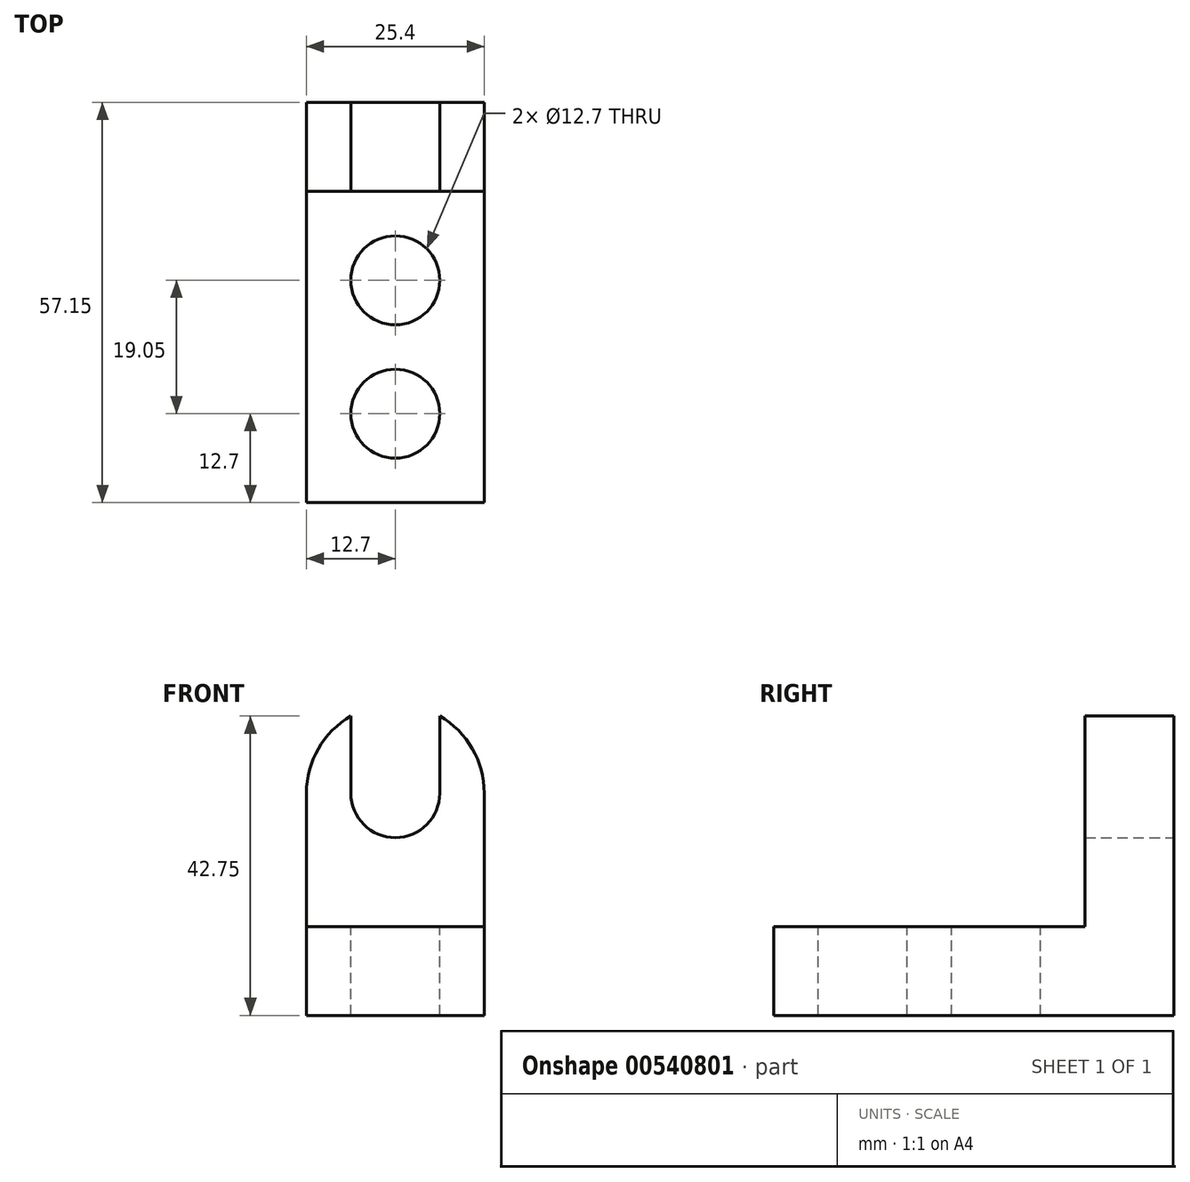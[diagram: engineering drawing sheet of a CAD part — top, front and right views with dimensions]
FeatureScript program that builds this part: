
annotation { "Feature Type Name" : "Feature", "Feature Type Description" : "" }
export const myFeature = defineFeature(function(context is Context, id is Id, definition is map)
    precondition{}
    {
        {
            var Q0;
            Q0=qCreatedBy(makeId("Top.planeOp"),FACE);
            var sketch = newSketch(context, id + "F0", { "sketchPlane" : qUnion([Q0])});
            skLineSegment(sketch, "E0", {"start": v(0, 0) * mm, "end": v(0, 57.15) * mm});
            skLineSegment(sketch, "E1", {"start": v(0, 57.15) * mm, "end": v(25.4, 57.15) * mm});
            skLineSegment(sketch, "E2", {"start": v(25.4, 57.15) * mm, "end": v(25.4, 0) * mm});
            skLineSegment(sketch, "E3", {"start": v(25.4, 0) * mm, "end": v(0, 0) * mm});
            skSolve(sketch);
        }
        {
            var Q0;
            Q0=makeQuery(id+"F0.imprint","IMPRINT",FACE,{"disambiguationData":[TD([[makeQuery(id+"F0.imprint","IMPRINT",EDGE,{"derivedFrom":sQuery(id+"F0.wireOp",EDGE,"E0")}),-1.0]])]});
            extrude(context, id + "F1", {"entities" : qUnion([Q0]), "depth" : 44.45 * mm, "offsetDistance" : 25.4 * mm});
        }
        {
            var Q0;
            Q0=makeQuery(id+"F1.opExtrude","SWEPT_FACE",FACE,{"disambiguationData":[OSD([sQuery(id+"F0.wireOp",EDGE,"E0")])]});
            var sketch = newSketch(context, id + "F2", { "sketchPlane" : qUnion([Q0])});
            skLineSegment(sketch, "E4", {"start": v(-44.45, 44.45) * mm, "end": v(-44.45, 12.7) * mm});
            skLineSegment(sketch, "E5", {"start": v(-44.45, 12.7) * mm, "end": v(0, 12.7) * mm});
            skLineSegment(sketch, "E6", {"start": v(0, 12.7) * mm, "end": v(0, 44.45) * mm});
            skLineSegment(sketch, "E7", {"start": v(0, 44.45) * mm, "end": v(-44.45, 44.45) * mm});
            skSolve(sketch);
        }
        {
            var Q0;
            Q0=makeQuery(id+"F2.imprint","IMPRINT",FACE,{"disambiguationData":[TD([[makeQuery(id+"F2.imprint","IMPRINT",EDGE,{"derivedFrom":sQuery(id+"F2.wireOp",EDGE,"E4")}),1.0]])]});
            extrude(context, id + "F3", {"entities" : qUnion([Q0]), "operationType" : NewBodyOperationType.REMOVE, "oppositeDirection" : true, "depth" : 25.4 * mm, "offsetDistance" : 25.4 * mm});
        }
        {
            var Q0;
            Q0=makeQuery(id+"F1.opExtrude","SWEPT_FACE",FACE,{"disambiguationData":[OSD([sQuery(id+"F0.wireOp",EDGE,"E1")])]});
            var sketch = newSketch(context, id + "F4", { "sketchPlane" : qUnion([Q0])});
            skArc(sketch, "E8", {"start": v(0, 31.75) * mm, "mid": v(-12.7, 44.45) * mm, "end": v(-25.4, 31.75) * mm});
            skSolve(sketch);
        }
        {
            var Q0;
            Q0 = qSketchRegion(id + "F4", true);
            var Q1;
            {var subQ0=sQuery(id+"F4.wireOp",EDGE,"E8");var subQ1=sQuery(id+"F0.wireOp",EDGE,"E1");var subQ4=makeQuery(id+"F1.opExtrude","CAP_EDGE",EDGE,{"disambiguationData":[OSD([subQ1])],"isStart":false});var subQ5=makeQuery(id+"F4.imprint","INTERSECT",VERTEX,{"derivedFrom":[subQ4,subQ0]});Q1=makeQuery(id+"F4.imprint","IMPRINT",FACE,{"disambiguationData":[TD([[makeQuery(id+"F4.imprint","IMPRINT",EDGE,{"disambiguationData":[TD([[subQ5,-1.0]])],"derivedFrom":subQ0}),-1.0]])]});}
            var Q2;
            {var subQ0=sQuery(id+"F4.wireOp",EDGE,"E8");var subQ1=sQuery(id+"F0.wireOp",EDGE,"E1");var subQ4=makeQuery(id+"F1.opExtrude","CAP_EDGE",EDGE,{"disambiguationData":[OSD([subQ1])],"isStart":false});var subQ5=makeQuery(id+"F4.imprint","INTERSECT",VERTEX,{"derivedFrom":[subQ4,subQ0]});Q2=makeQuery(id+"F4.imprint","IMPRINT",FACE,{"disambiguationData":[TD([[makeQuery(id+"F4.imprint","IMPRINT",EDGE,{"disambiguationData":[TD([[subQ5,1.0]])],"derivedFrom":subQ0}),-1.0]])]});}
            extrude(context, id + "F5", {"entities" : qUnion([Q0, Q1, Q2]), "operationType" : NewBodyOperationType.REMOVE, "oppositeDirection" : true, "depth" : 25.4 * mm, "offsetDistance" : 25.4 * mm});
        }
        {
            var Q0;
            Q0=makeQuery(id+"F1.opExtrude","SWEPT_FACE",FACE,{"disambiguationData":[OSD([sQuery(id+"F0.wireOp",EDGE,"E1")])]});
            var sketch = newSketch(context, id + "F6", { "sketchPlane" : qUnion([Q0])});
            skEllipse(sketch, "E9", {"center": v(-12.7, 31.75) * mm, "majorRadius": 6.35 * mm, "minorRadius": 6.35 * mm, "majorAxis": v(1, 0)});
            skLineSegment(sketch, "E10", {"start": v(-19.05, 31.75) * mm, "end": v(-19.05, 51.32) * mm});
            skPoint(sketch, "E11.endSnap0", {"position": v(-6.35, 31.75) * mm});
            skLineSegment(sketch, "E12", {"start": v(-6.35, 51.32) * mm, "end": v(-6.35, 31.75) * mm});
            skSolve(sketch);
        }
        {
            var Q0;
            {var subQ0=sQuery(id+"F6.wireOp",EDGE,"E10");var subQ1=sQuery(id+"F6.wireOp",EDGE,"E9");var subQ2=makeQuery(id+"F6.imprint","INTERSECT",VERTEX,{"derivedFrom":[subQ1,subQ0]});Q0=makeQuery(id+"F6.imprint","IMPRINT",FACE,{"disambiguationData":[TD([[makeQuery(id+"F6.imprint","IMPRINT",EDGE,{"disambiguationData":[TD([[subQ2,1.0]])],"derivedFrom":subQ1}),-1.0]])]});}
            var Q1;
            {var subQ0=sQuery(id+"F6.wireOp",EDGE,"E9");var subQ1=makeQuery(id+"F6.imprint","INTERSECT",VERTEX,{"derivedFrom":[subQ0,sQuery(id+"F6.wireOp",EDGE,"E10")]});Q1=makeQuery(id+"F6.imprint","IMPRINT",FACE,{"disambiguationData":[TD([[makeQuery(id+"F6.imprint","IMPRINT",EDGE,{"disambiguationData":[TD([[subQ1,1.0]])],"derivedFrom":subQ0}),1.0]])]});}
            extrude(context, id + "F7", {"entities" : qUnion([Q0, Q1]), "operationType" : NewBodyOperationType.REMOVE, "oppositeDirection" : true, "depth" : 25.4 * mm, "offsetDistance" : 25.4 * mm});
        }
        {
            var Q0;
            Q0=makeQuery(id+"F3.boolean.opBoolean","COPY",FACE,{"derivedFrom":makeQuery(id+"F3.opExtrude","SWEPT_FACE",FACE,{"disambiguationData":[OSD([sQuery(id+"F2.wireOp",EDGE,"E5")])]})});
            var sketch = newSketch(context, id + "F8", { "sketchPlane" : qUnion([Q0])});
            skCircle(sketch, "E13", {"center": v(12.7, 31.75) * mm, "radius": 6.35 * mm});
            skCircle(sketch, "E14", {"center": v(12.7, 12.7) * mm, "radius": 6.35 * mm});
            skSolve(sketch);
        }
        {
            var Q0;
            Q0 = qSketchRegion(id + "F8", true);
            extrude(context, id + "F9", {"entities" : qUnion([Q0]), "operationType" : NewBodyOperationType.REMOVE, "oppositeDirection" : true, "depth" : 25.4 * mm, "offsetDistance" : 25.4 * mm});
        }
    });
